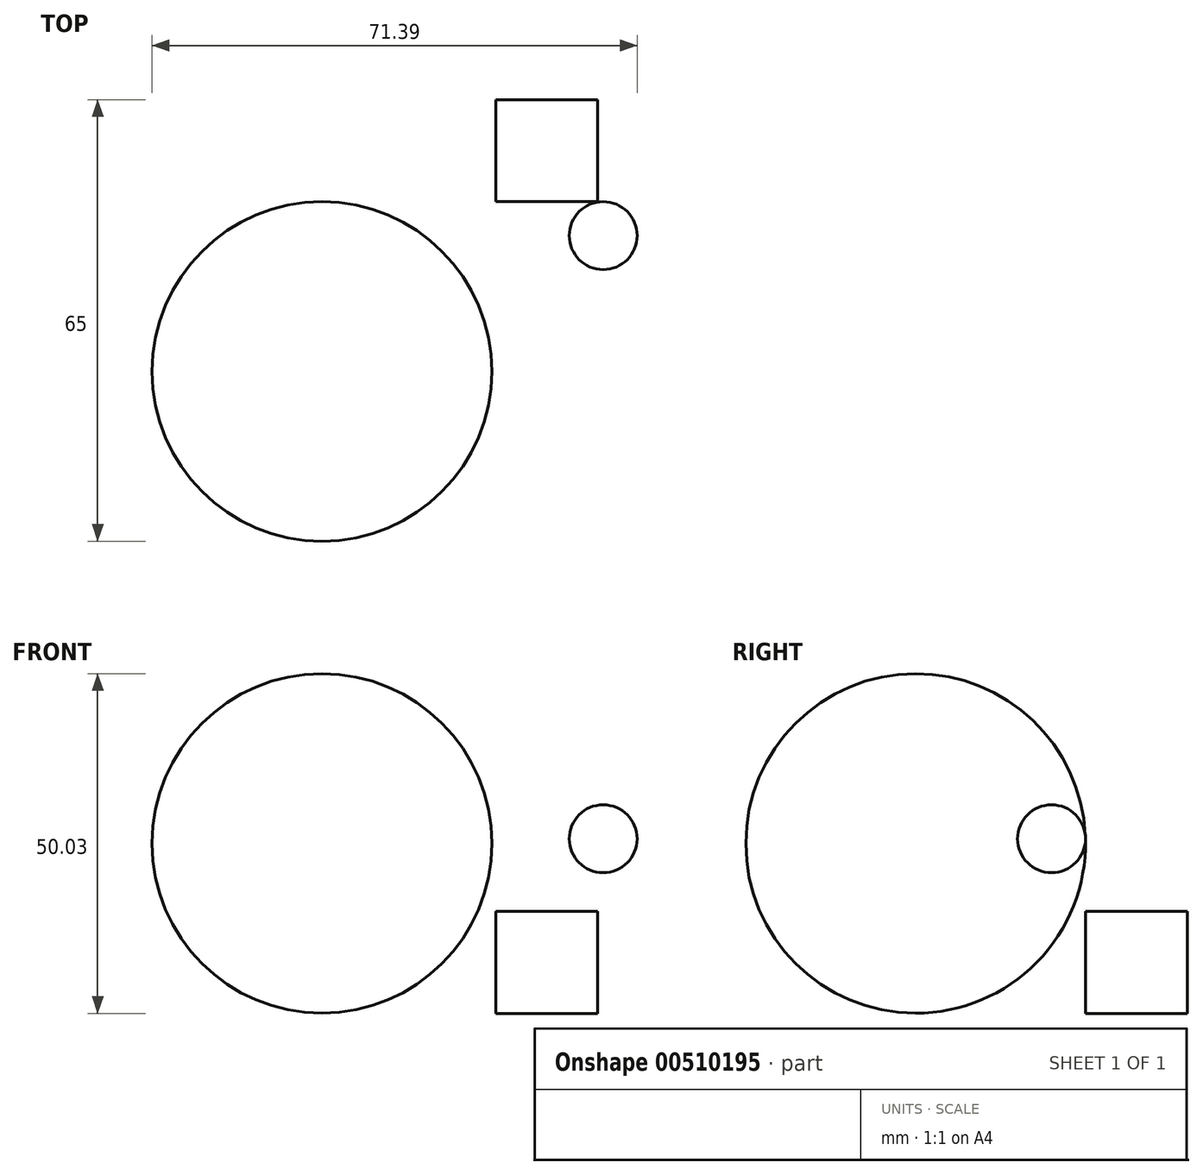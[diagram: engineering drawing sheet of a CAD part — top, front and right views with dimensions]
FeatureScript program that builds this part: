
annotation { "Feature Type Name" : "Feature", "Feature Type Description" : "" }
export const myFeature = defineFeature(function(context is Context, id is Id, definition is map)
    precondition{}
    {
        {
            var Q0;
            Q0=qCreatedBy(makeId("Front.planeOp"),FACE);
            var sketch = newSketch(context, id + "F0", { "sketchPlane" : qUnion([Q0])});
            skLineSegment(sketch, "E0.bottom", {"start": v(-17.7, 50.03) * mm, "end": v(32.3, 50.03) * mm});
            skLineSegment(sketch, "E0.top", {"start": v(-17.7, 0.03) * mm, "end": v(32.3, 0.03) * mm});
            skLineSegment(sketch, "E0.left", {"start": v(-17.7, 50.03) * mm, "end": v(-17.7, 0.03) * mm});
            skLineSegment(sketch, "E0.right", {"start": v(32.3, 50.03) * mm, "end": v(32.3, 0.03) * mm});
            skSolve(sketch);
        }
        {
            var Q0;
            Q0=makeQuery(id+"F0.imprint","IMPRINT",FACE,{"disambiguationData":[TD([[makeQuery(id+"F0.imprint","IMPRINT",EDGE,{"derivedFrom":sQuery(id+"F0.wireOp",EDGE,"E0.bottom")}),-1.0]])]});
            extrude(context, id + "F1", {"entities" : qUnion([Q0]), "depth" : 50 * mm});
        }
        {
            var Q0;
            Q0=makeQuery(id+"F1.opExtrude","SWEPT_EDGE",EDGE,{"disambiguationData":[OSD([sQuery(id+"F0.wireOp",EDGE,"E0.bottom"),sQuery(id+"F0.wireOp",EDGE,"E0.left")])]});
            var Q1;
            Q1=makeQuery(id+"F1.opExtrude","SWEPT_FACE",FACE,{"disambiguationData":[OSD([sQuery(id+"F0.wireOp",EDGE,"E0.bottom")])]});
            var Q2;
            Q2=makeQuery(id+"F1.opExtrude","SWEPT_EDGE",EDGE,{"disambiguationData":[OSD([sQuery(id+"F0.wireOp",EDGE,"E0.bottom"),sQuery(id+"F0.wireOp",EDGE,"E0.right")])]});
            var Q3;
            Q3=makeQuery(id+"F1.opExtrude","CAP_FACE",FACE,{"disambiguationData":[OSD([sQuery(id+"F0.wireOp",EDGE,"E0.bottom"),sQuery(id+"F0.wireOp",EDGE,"E0.top"),sQuery(id+"F0.wireOp",EDGE,"E0.left"),sQuery(id+"F0.wireOp",EDGE,"E0.right")])],"isStart":true});
            var Q4;
            Q4=makeQuery(id+"F1.opExtrude","CAP_FACE",FACE,{"disambiguationData":[OSD([sQuery(id+"F0.wireOp",EDGE,"E0.bottom"),sQuery(id+"F0.wireOp",EDGE,"E0.top"),sQuery(id+"F0.wireOp",EDGE,"E0.left"),sQuery(id+"F0.wireOp",EDGE,"E0.right")])],"isStart":false});
            var Q5;
            Q5=makeQuery(id+"F1.opExtrude","SWEPT_EDGE",EDGE,{"disambiguationData":[OSD([sQuery(id+"F0.wireOp",EDGE,"E0.top"),sQuery(id+"F0.wireOp",EDGE,"E0.right")])]});
            var Q6;
            Q6=makeQuery(id+"F1.opExtrude","SWEPT_FACE",FACE,{"disambiguationData":[OSD([sQuery(id+"F0.wireOp",EDGE,"E0.top")])]});
            var Q7;
            Q7=makeQuery(id+"F1.opExtrude","SWEPT_FACE",FACE,{"disambiguationData":[OSD([sQuery(id+"F0.wireOp",EDGE,"E0.right")])]});
            var Q8;
            Q8=makeQuery(id+"F1.opExtrude","SWEPT_EDGE",EDGE,{"disambiguationData":[OSD([sQuery(id+"F0.wireOp",EDGE,"E0.top"),sQuery(id+"F0.wireOp",EDGE,"E0.left")])]});
            var Q9;
            Q9=makeQuery(id+"F1.opExtrude","CAP_EDGE",EDGE,{"disambiguationData":[OSD([sQuery(id+"F0.wireOp",EDGE,"E0.bottom")])],"isStart":true});
            var Q10;
            Q10=makeQuery(id+"F1.opExtrude","SWEPT_FACE",FACE,{"disambiguationData":[OSD([sQuery(id+"F0.wireOp",EDGE,"E0.left")])]});
            var Q11;
            Q11=makeQuery(id+"F1.opExtrude","CAP_EDGE",EDGE,{"disambiguationData":[OSD([sQuery(id+"F0.wireOp",EDGE,"E0.bottom")])],"isStart":false});
            var Q12;
            Q12=makeQuery(id+"F1.opExtrude","CAP_EDGE",EDGE,{"disambiguationData":[OSD([sQuery(id+"F0.wireOp",EDGE,"E0.top")])],"isStart":true});
            var Q13;
            Q13=makeQuery(id+"F1.opExtrude","CAP_EDGE",EDGE,{"disambiguationData":[OSD([sQuery(id+"F0.wireOp",EDGE,"E0.top")])],"isStart":false});
            var Q14;
            Q14=makeQuery(id+"F1.opExtrude","CAP_EDGE",EDGE,{"disambiguationData":[OSD([sQuery(id+"F0.wireOp",EDGE,"E0.right")])],"isStart":true});
            var Q15;
            Q15=makeQuery(id+"F1.opExtrude","CAP_EDGE",EDGE,{"disambiguationData":[OSD([sQuery(id+"F0.wireOp",EDGE,"E0.right")])],"isStart":false});
            var Q16;
            Q16=makeQuery(id+"F1.opExtrude","CAP_EDGE",EDGE,{"disambiguationData":[OSD([sQuery(id+"F0.wireOp",EDGE,"E0.left")])],"isStart":true});
            var Q17;
            Q17=makeQuery(id+"F1.opExtrude","CAP_EDGE",EDGE,{"disambiguationData":[OSD([sQuery(id+"F0.wireOp",EDGE,"E0.left")])],"isStart":false});
            fillet(context, id + "F2", {"entities" : qUnion([Q0, Q1, Q2, Q3, Q4, Q5, Q6, Q7, Q8, Q9, Q10, Q11, Q12, Q13, Q14, Q15, Q16, Q17]), "radius" : 25 * mm, "tangentPropagation" : true, "allowEdgeOverflow" : false});
        }
        {
            var Q0;
            Q0=qCreatedBy(makeId("Front.planeOp"),FACE);
            var sketch = newSketch(context, id + "F3", { "sketchPlane" : qUnion([Q0])});
            skLineSegment(sketch, "E1.bottom", {"start": v(43.68, 30.7) * mm, "end": v(53.68, 30.7) * mm});
            skLineSegment(sketch, "E1.top", {"start": v(43.68, 20.7) * mm, "end": v(53.68, 20.7) * mm});
            skLineSegment(sketch, "E1.left", {"start": v(43.68, 30.7) * mm, "end": v(43.68, 20.7) * mm});
            skLineSegment(sketch, "E1.right", {"start": v(53.68, 30.7) * mm, "end": v(53.68, 20.7) * mm});
            skSolve(sketch);
        }
        {
            var Q0;
            Q0=makeQuery(id+"F3.imprint","IMPRINT",FACE,{"disambiguationData":[TD([[makeQuery(id+"F3.imprint","IMPRINT",EDGE,{"derivedFrom":sQuery(id+"F3.wireOp",EDGE,"E1.bottom")}),-1.0]])]});
            extrude(context, id + "F4", {"entities" : qUnion([Q0]), "depth" : 10 * mm});
        }
        {
            var Q0;
            Q0=makeQuery(id+"F4.opExtrude","SWEPT_FACE",FACE,{"disambiguationData":[OSD([sQuery(id+"F3.wireOp",EDGE,"E1.right")])]});
            var Q1;
            Q1=makeQuery(id+"F4.opExtrude","SWEPT_FACE",FACE,{"disambiguationData":[OSD([sQuery(id+"F3.wireOp",EDGE,"E1.bottom")])]});
            var Q2;
            Q2=makeQuery(id+"F4.opExtrude","CAP_FACE",FACE,{"disambiguationData":[OSD([sQuery(id+"F3.wireOp",EDGE,"E1.bottom"),sQuery(id+"F3.wireOp",EDGE,"E1.top"),sQuery(id+"F3.wireOp",EDGE,"E1.left"),sQuery(id+"F3.wireOp",EDGE,"E1.right")])],"isStart":false});
            var Q3;
            Q3=makeQuery(id+"F4.opExtrude","SWEPT_EDGE",EDGE,{"disambiguationData":[OSD([sQuery(id+"F3.wireOp",EDGE,"E1.top"),sQuery(id+"F3.wireOp",EDGE,"E1.right")])]});
            var Q4;
            Q4=makeQuery(id+"F4.opExtrude","CAP_EDGE",EDGE,{"disambiguationData":[OSD([sQuery(id+"F3.wireOp",EDGE,"E1.top")])],"isStart":false});
            var Q5;
            Q5=makeQuery(id+"F4.opExtrude","SWEPT_EDGE",EDGE,{"disambiguationData":[OSD([sQuery(id+"F3.wireOp",EDGE,"E1.bottom"),sQuery(id+"F3.wireOp",EDGE,"E1.left")])]});
            var Q6;
            Q6=makeQuery(id+"F4.opExtrude","SWEPT_FACE",FACE,{"disambiguationData":[OSD([sQuery(id+"F3.wireOp",EDGE,"E1.top")])]});
            var Q7;
            Q7=makeQuery(id+"F4.opExtrude","CAP_EDGE",EDGE,{"disambiguationData":[OSD([sQuery(id+"F3.wireOp",EDGE,"E1.bottom")])],"isStart":true});
            var Q8;
            Q8=makeQuery(id+"F4.opExtrude","SWEPT_EDGE",EDGE,{"disambiguationData":[OSD([sQuery(id+"F3.wireOp",EDGE,"E1.bottom"),sQuery(id+"F3.wireOp",EDGE,"E1.right")])]});
            var Q9;
            Q9=makeQuery(id+"F4.opExtrude","CAP_FACE",FACE,{"disambiguationData":[OSD([sQuery(id+"F3.wireOp",EDGE,"E1.bottom"),sQuery(id+"F3.wireOp",EDGE,"E1.top"),sQuery(id+"F3.wireOp",EDGE,"E1.left"),sQuery(id+"F3.wireOp",EDGE,"E1.right")])],"isStart":true});
            var Q10;
            Q10=makeQuery(id+"F4.opExtrude","CAP_EDGE",EDGE,{"disambiguationData":[OSD([sQuery(id+"F3.wireOp",EDGE,"E1.bottom")])],"isStart":false});
            var Q11;
            Q11=makeQuery(id+"F4.opExtrude","CAP_EDGE",EDGE,{"disambiguationData":[OSD([sQuery(id+"F3.wireOp",EDGE,"E1.right")])],"isStart":false});
            var Q12;
            Q12=makeQuery(id+"F4.opExtrude","CAP_EDGE",EDGE,{"disambiguationData":[OSD([sQuery(id+"F3.wireOp",EDGE,"E1.top")])],"isStart":true});
            var Q13;
            Q13=makeQuery(id+"F4.opExtrude","SWEPT_EDGE",EDGE,{"disambiguationData":[OSD([sQuery(id+"F3.wireOp",EDGE,"E1.top"),sQuery(id+"F3.wireOp",EDGE,"E1.left")])]});
            var Q14;
            Q14=makeQuery(id+"F4.opExtrude","SWEPT_FACE",FACE,{"disambiguationData":[OSD([sQuery(id+"F3.wireOp",EDGE,"E1.left")])]});
            var Q15;
            Q15=makeQuery(id+"F4.opExtrude","CAP_EDGE",EDGE,{"disambiguationData":[OSD([sQuery(id+"F3.wireOp",EDGE,"E1.right")])],"isStart":true});
            var Q16;
            Q16=makeQuery(id+"F4.opExtrude","CAP_EDGE",EDGE,{"disambiguationData":[OSD([sQuery(id+"F3.wireOp",EDGE,"E1.left")])],"isStart":false});
            var Q17;
            Q17=makeQuery(id+"F4.opExtrude","CAP_EDGE",EDGE,{"disambiguationData":[OSD([sQuery(id+"F3.wireOp",EDGE,"E1.left")])],"isStart":true});
            fillet(context, id + "F5", {"entities" : qUnion([Q0, Q1, Q2, Q3, Q4, Q5, Q6, Q7, Q8, Q9, Q10, Q11, Q12, Q13, Q14, Q15, Q16, Q17]), "radius" : 5 * mm, "tangentPropagation" : true, "allowEdgeOverflow" : false});
        }
        {
            var Q0;
            Q0=qCreatedBy(makeId("Top.planeOp"),FACE);
            var sketch = newSketch(context, id + "F6", { "sketchPlane" : qUnion([Q0])});
            skLineSegment(sketch, "E2.bottom", {"start": v(32.9, 15) * mm, "end": v(47.9, 15) * mm});
            skLineSegment(sketch, "E2.top", {"start": v(32.9, 0) * mm, "end": v(47.9, 0) * mm});
            skLineSegment(sketch, "E2.left", {"start": v(32.9, 15) * mm, "end": v(32.9, 0) * mm});
            skLineSegment(sketch, "E2.right", {"start": v(47.9, 15) * mm, "end": v(47.9, 0) * mm});
            skSolve(sketch);
        }
        {
            var Q0;
            Q0=makeQuery(id+"F6.imprint","IMPRINT",FACE,{"disambiguationData":[TD([[makeQuery(id+"F6.imprint","IMPRINT",EDGE,{"derivedFrom":sQuery(id+"F6.wireOp",EDGE,"E2.bottom")}),-1.0]])]});
            extrude(context, id + "F7", {"entities" : qUnion([Q0]), "depth" : 15 * mm});
        }
    });
